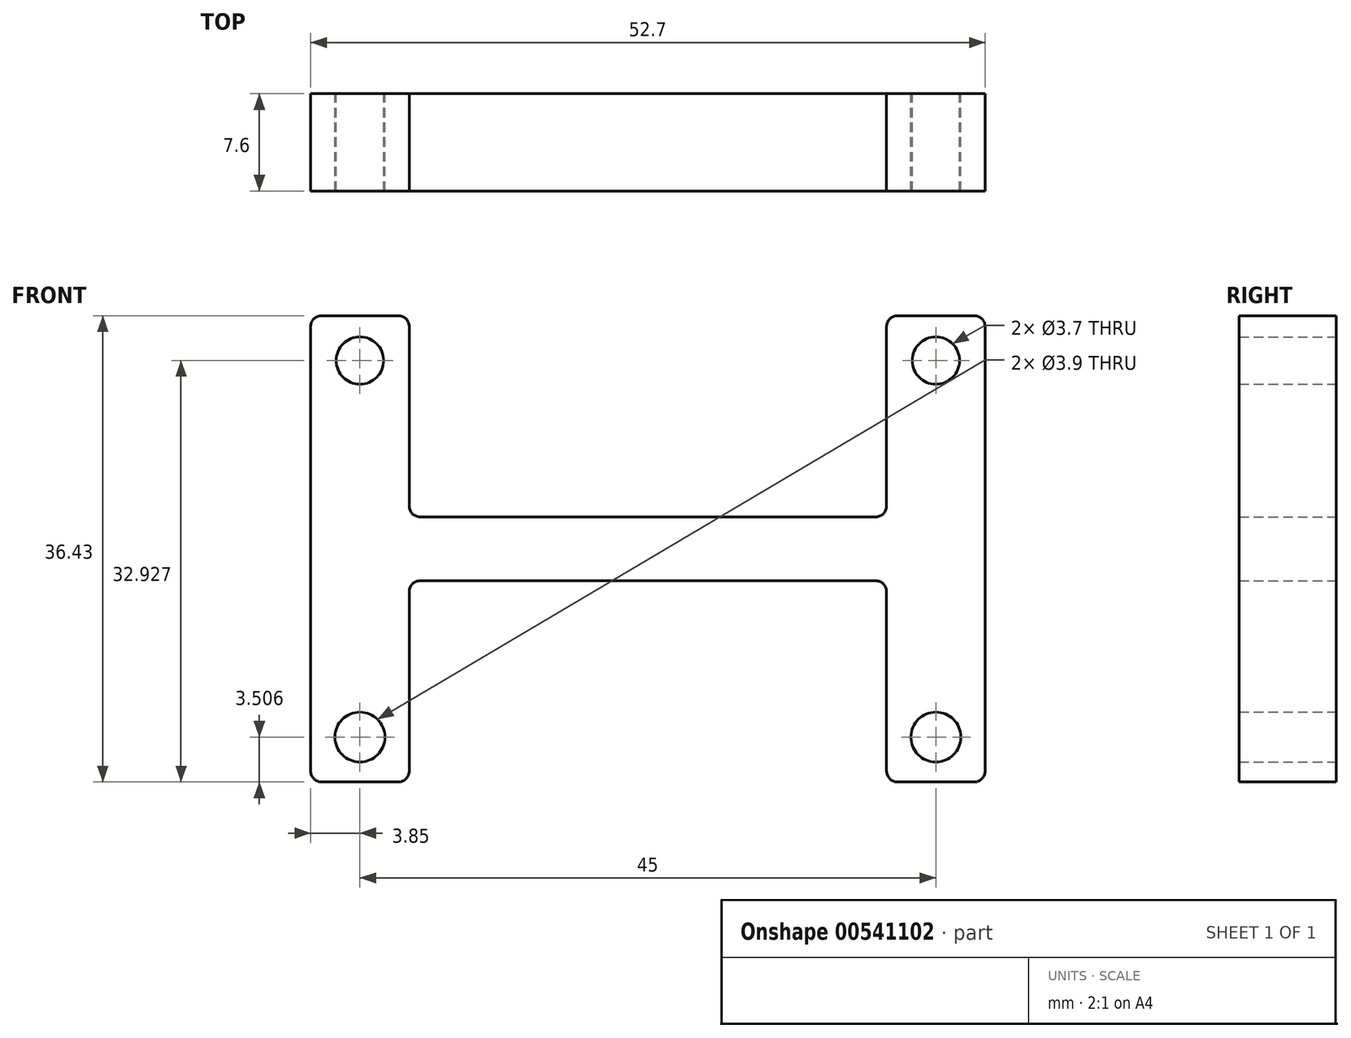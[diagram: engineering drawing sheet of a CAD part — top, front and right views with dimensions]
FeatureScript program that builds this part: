
annotation { "Feature Type Name" : "Feature", "Feature Type Description" : "" }
export const myFeature = defineFeature(function(context is Context, id is Id, definition is map)
    precondition{}
    {
        {
            var Q0;
            Q0=qCreatedBy(makeId("Front.planeOp"),FACE);
            var sketch = newSketch(context, id + "F0", { "sketchPlane" : qUnion([Q0])});
            skLineSegment(sketch, "E0", {"start": v(-26.35, 0.85) * mm, "end": v(-26.35, 35.58) * mm});
            skLineSegment(sketch, "E1", {"start": v(-25.5, 36.43) * mm, "end": v(-19.5, 36.43) * mm});
            skLineSegment(sketch, "E2", {"start": v(-18.65, 21.57) * mm, "end": v(-18.65, 35.58) * mm});
            skLineSegment(sketch, "E3", {"start": v(-19.5, 0) * mm, "end": v(-25.5, 0) * mm});
            skPoint(sketch, "E4.visualSharp", {"position": v(-26.35, 36.43) * mm});
            skArc(sketch, "E4.filletArc", {"start": v(-25.5, 36.43) * mm, "mid": v(-26.1, 36.18) * mm, "end": v(-26.35, 35.58) * mm});
            skPoint(sketch, "E5.visualSharp", {"position": v(-18.65, 36.43) * mm});
            skArc(sketch, "E5.filletArc", {"start": v(-18.65, 35.58) * mm, "mid": v(-18.9, 36.18) * mm, "end": v(-19.5, 36.43) * mm});
            skPoint(sketch, "E6.visualSharp", {"position": v(-26.35, 0) * mm});
            skArc(sketch, "E6.filletArc", {"start": v(-26.35, 0.85) * mm, "mid": v(-26.1, 0.25) * mm, "end": v(-25.5, 0) * mm});
            skPoint(sketch, "E7.visualSharp", {"position": v(-18.65, 0) * mm});
            skArc(sketch, "E7.filletArc", {"start": v(-19.5, 0) * mm, "mid": v(-18.9, 0.25) * mm, "end": v(-18.65, 0.85) * mm});
            skLineSegment(sketch, "E8", {"start": v(-22.5, 36.43) * mm, "end": v(-22.5, 32.93) * mm, "construction": true});
            skCircle(sketch, "E9", {"center": v(-22.5, 32.93) * mm, "radius": 1.85 * mm});
            skCircle(sketch, "E10", {"center": v(-22.5, 3.5) * mm, "radius": 1.95 * mm});
            skLineSegment(sketch, "E11", {"start": v(-22.5, 32.93) * mm, "end": v(-22.5, 3.5) * mm, "construction": true});
            skLineSegment(sketch, "E12", {"start": v(-22.5, 0) * mm, "end": v(-22.5, 3.5) * mm, "construction": true});
            skLineSegment(sketch, "E13.MirrorCS", {"start": v(26.35, 0.85) * mm, "end": v(26.35, 35.58) * mm});
            skLineSegment(sketch, "E14.MirrorCS", {"start": v(25.5, 36.43) * mm, "end": v(19.5, 36.43) * mm});
            skLineSegment(sketch, "E15.MirrorCS", {"start": v(18.65, 0.85) * mm, "end": v(18.65, 14.87) * mm});
            skPoint(sketch, "E16.MirrorP", {"position": v(18.65, 36.43) * mm});
            skPoint(sketch, "E17.MirrorP", {"position": v(26.35, 36.43) * mm});
            skLineSegment(sketch, "E18.MirrorCS", {"start": v(19.5, 0) * mm, "end": v(25.5, 0) * mm});
            skCircle(sketch, "E19.MirrorC", {"center": v(22.5, 3.5) * mm, "radius": 1.95 * mm});
            skCircle(sketch, "E20.MirrorC", {"center": v(22.5, 32.93) * mm, "radius": 1.85 * mm});
            skArc(sketch, "E21", {"start": v(18.65, 35.58) * mm, "mid": v(18.9, 36.18) * mm, "end": v(19.5, 36.43) * mm});
            skArc(sketch, "E22", {"start": v(26.35, 35.58) * mm, "mid": v(26.1, 36.18) * mm, "end": v(25.5, 36.43) * mm});
            skArc(sketch, "E23", {"start": v(18.65, 0.85) * mm, "mid": v(18.9, 0.25) * mm, "end": v(19.5, 0) * mm});
            skArc(sketch, "E24", {"start": v(25.5, 0) * mm, "mid": v(26.1, 0.25) * mm, "end": v(26.35, 0.85) * mm});
            skLineSegment(sketch, "E25", {"start": v(-18.65, 18.22) * mm, "end": v(18.65, 18.22) * mm, "construction": true});
            skLineSegment(sketch, "E26", {"start": v(-18.65, 18.22) * mm, "end": v(-18.65, 20.72) * mm, "construction": true});
            skLineSegment(sketch, "E27", {"start": v(-18.65, 18.22) * mm, "end": v(-18.65, 15.72) * mm, "construction": true});
            skLineSegment(sketch, "E28", {"start": v(-17.8, 20.72) * mm, "end": v(17.8, 20.72) * mm});
            skLineSegment(sketch, "E29", {"start": v(-17.8, 15.72) * mm, "end": v(17.8, 15.72) * mm});
            skPoint(sketch, "E30.newPointA", {"position": v(-18.65, 0.85) * mm});
            skArc(sketch, "E30.filletArc", {"start": v(-18.65, 21.57) * mm, "mid": v(-18.4, 20.96) * mm, "end": v(-17.8, 20.72) * mm});
            skLineSegment(sketch, "E31", {"start": v(-18.65, 14.87) * mm, "end": v(-18.65, 0.85) * mm});
            skPoint(sketch, "E32.visualSharp", {"position": v(-18.65, 15.72) * mm});
            skArc(sketch, "E32.filletArc", {"start": v(-17.8, 15.72) * mm, "mid": v(-18.4, 15.47) * mm, "end": v(-18.65, 14.87) * mm});
            skPoint(sketch, "E33.newPointB", {"position": v(18.65, 35.58) * mm});
            skArc(sketch, "E33.filletArc", {"start": v(18.65, 14.87) * mm, "mid": v(18.4, 15.47) * mm, "end": v(17.8, 15.72) * mm});
            skLineSegment(sketch, "E34", {"start": v(18.65, 35.58) * mm, "end": v(18.65, 21.57) * mm});
            skPoint(sketch, "E35.visualSharp", {"position": v(18.65, 20.72) * mm});
            skArc(sketch, "E35.filletArc", {"start": v(17.8, 20.72) * mm, "mid": v(18.4, 20.96) * mm, "end": v(18.65, 21.57) * mm});
            skLineSegment(sketch, "E36", {"start": v(17.8, 20.72) * mm, "end": v(26.35, 20.72) * mm, "construction": true});
            skSolve(sketch);
        }
        {
            var Q0;
            Q0=makeQuery(id+"F0.imprint","IMPRINT",FACE,{"disambiguationData":[TD([[makeQuery(id+"F0.imprint","IMPRINT",EDGE,{"derivedFrom":sQuery(id+"F0.wireOp",EDGE,"E0")}),-1.0]])]});
            extrude(context, id + "F1", {"entities" : qUnion([Q0]), "depth" : 7.6 * mm, "offsetDistance" : 25 * mm});
        }
    });
